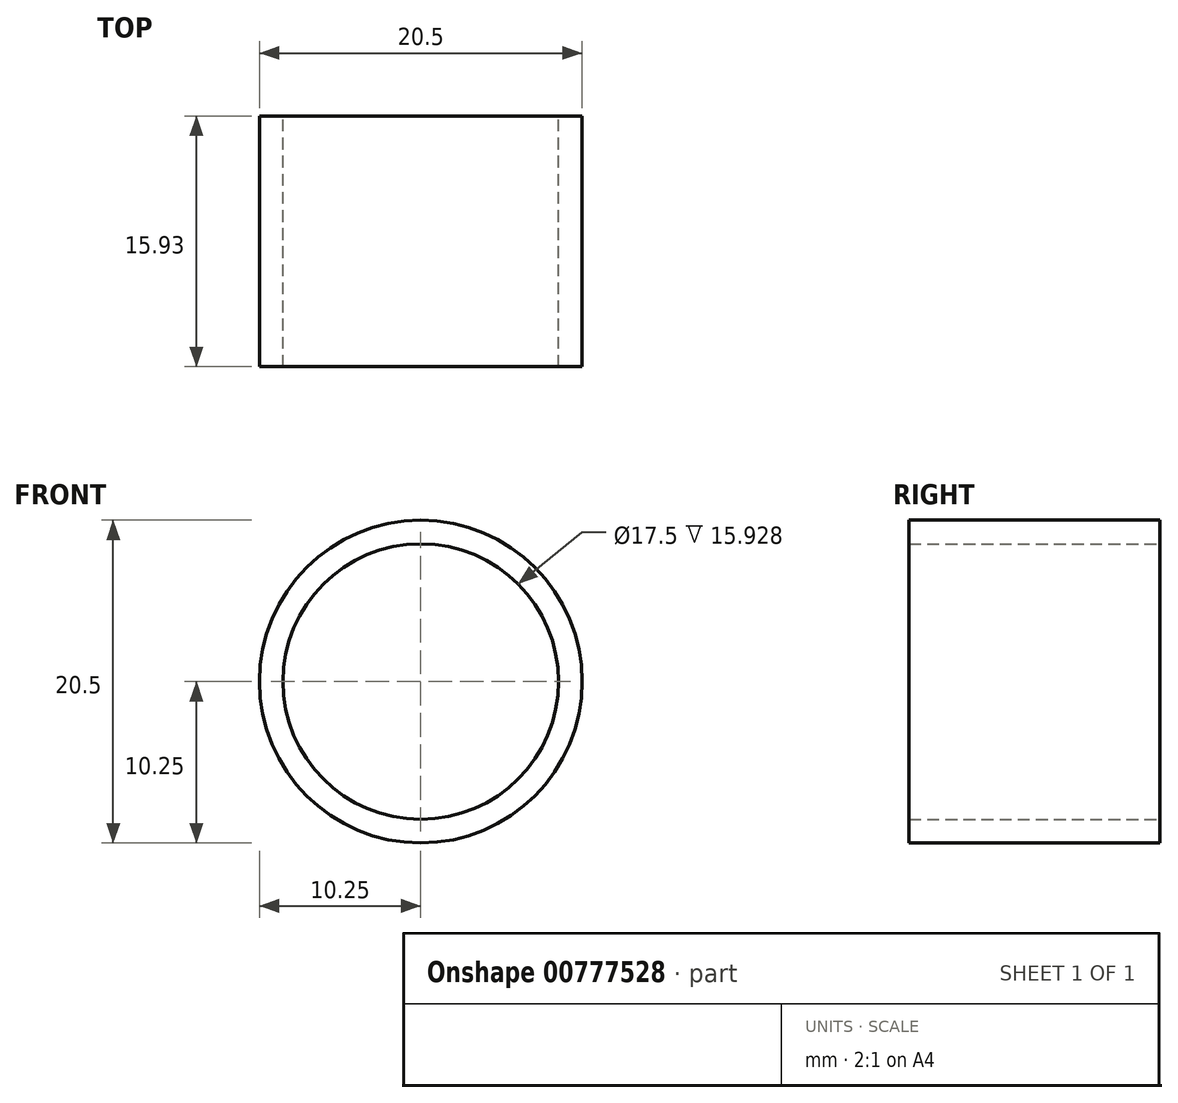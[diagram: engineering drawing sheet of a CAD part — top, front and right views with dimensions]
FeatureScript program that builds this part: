
annotation { "Feature Type Name" : "Feature", "Feature Type Description" : "" }
export const myFeature = defineFeature(function(context is Context, id is Id, definition is map)
    precondition{}
    {
        {
            var Q0;
            Q0=qCreatedBy(makeId("Front.planeOp"),FACE);
            var sketch = newSketch(context, id + "F0", { "sketchPlane" : qUnion([Q0])});
            skCircle(sketch, "E0", {"center": v(0, 0) * mm, "radius": 10.25 * mm});
            skCircle(sketch, "E1", {"center": v(0, 0) * mm, "radius": 8.75 * mm});
            skLineSegment(sketch, "E2", {"start": v(0, 0) * mm, "end": v(0, 8.75) * mm, "construction": true});
            skSolve(sketch);
        }
        {
            var Q0;
            Q0 = qSketchRegion(id + "F0", true);
            extrude(context, id + "F1", {"entities" : qUnion([Q0]), "depth" : 15.93 * mm, "offsetDistance" : 25 * mm});
        }
    });
